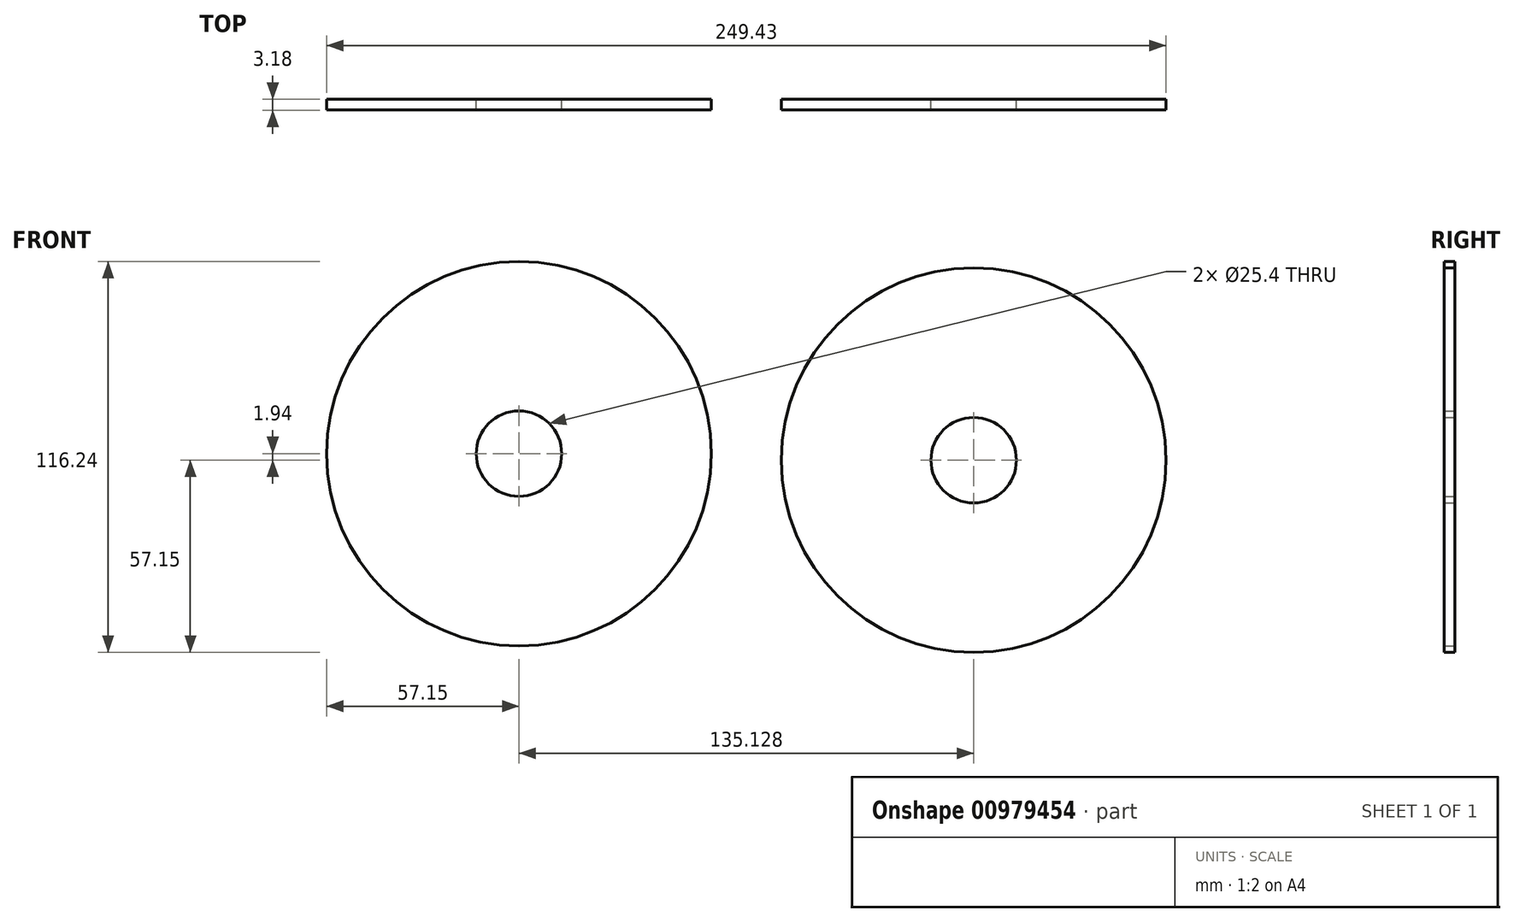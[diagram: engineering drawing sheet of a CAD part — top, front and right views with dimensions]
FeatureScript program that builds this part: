
annotation { "Feature Type Name" : "Feature", "Feature Type Description" : "" }
export const myFeature = defineFeature(function(context is Context, id is Id, definition is map)
    precondition{}
    {
        {
            var Q0;
            Q0=qCreatedBy(makeId("Front.planeOp"),FACE);
            var sketch = newSketch(context, id + "F0", { "sketchPlane" : qUnion([Q0])});
            skCircle(sketch, "E0", {"center": v(0, 0) * mm, "radius": 57.15 * mm});
            skLineSegment(sketch, "E1", {"start": v(-32.13, 47.26) * mm, "end": v(-11.2, 16.47) * mm});
            skLineSegment(sketch, "E2", {"start": v(6.27, 18.9) * mm, "end": v(18, 54.24) * mm});
            skLineSegment(sketch, "E3", {"start": v(18, 54.24) * mm, "end": v(6.27, 18.9) * mm});
            skLineSegment(sketch, "E4", {"start": v(10.46, -16.95) * mm, "end": v(24.43, -51.66) * mm});
            skLineSegment(sketch, "E5", {"start": v(24.43, -51.66) * mm, "end": v(10.46, -16.95) * mm});
            skLineSegment(sketch, "E6", {"start": v(-19.91, 0) * mm, "end": v(-57.15, 0) * mm});
            skLineSegment(sketch, "E7", {"start": v(-57.15, 0) * mm, "end": v(-19.91, 0) * mm});
            skLineSegment(sketch, "E8", {"start": v(19.91, 0) * mm, "end": v(57.15, 0) * mm});
            skLineSegment(sketch, "E9", {"start": v(57.15, 0) * mm, "end": v(19.91, 0) * mm});
            skLineSegment(sketch, "E10", {"start": v(-9.2, -17.66) * mm, "end": v(-27.3, -50.21) * mm});
            skLineSegment(sketch, "E11", {"start": v(-27.3, -50.21) * mm, "end": v(-9.2, -17.66) * mm});
            skCircle(sketch, "E12", {"center": v(135.13, -1.94) * mm, "radius": 57.15 * mm});
            skLineSegment(sketch, "E13", {"start": v(103, 45.32) * mm, "end": v(123.93, 14.53) * mm});
            skLineSegment(sketch, "E14", {"start": v(141.4, 16.96) * mm, "end": v(153.12, 52.3) * mm});
            skLineSegment(sketch, "E15", {"start": v(153.12, 52.3) * mm, "end": v(141.4, 16.96) * mm});
            skLineSegment(sketch, "E16", {"start": v(145.58, -18.89) * mm, "end": v(159.56, -53.6) * mm});
            skLineSegment(sketch, "E17", {"start": v(159.56, -53.6) * mm, "end": v(145.58, -18.89) * mm});
            skLineSegment(sketch, "E18", {"start": v(115.22, -1.94) * mm, "end": v(77.98, -1.94) * mm});
            skLineSegment(sketch, "E19", {"start": v(77.98, -1.94) * mm, "end": v(115.22, -1.94) * mm});
            skLineSegment(sketch, "E20", {"start": v(155.04, -1.94) * mm, "end": v(192.28, -1.94) * mm});
            skLineSegment(sketch, "E21", {"start": v(192.28, -1.94) * mm, "end": v(155.04, -1.94) * mm});
            skLineSegment(sketch, "E22", {"start": v(125.93, -19.6) * mm, "end": v(107.84, -52.15) * mm});
            skLineSegment(sketch, "E23", {"start": v(107.84, -52.15) * mm, "end": v(125.93, -19.6) * mm});
            skCircle(sketch, "E24", {"center": v(0, 0) * mm, "radius": 12.7 * mm});
            skCircle(sketch, "E25", {"center": v(135.13, -1.94) * mm, "radius": 12.7 * mm});
            skSolve(sketch);
        }
        {
            var Q0;
            Q0=makeQuery(id+"F0.imprint","IMPRINT",FACE,{"disambiguationData":[TD([[makeQuery(id+"F0.imprint","IMPRINT",EDGE,{"derivedFrom":sQuery(id+"F0.wireOp",EDGE,"E24")}),-1.0]])]});
            var Q1;
            Q1=makeQuery(id+"F0.imprint","IMPRINT",FACE,{"disambiguationData":[TD([[makeQuery(id+"F0.imprint","IMPRINT",EDGE,{"derivedFrom":sQuery(id+"F0.wireOp",EDGE,"E25")}),-1.0]])]});
            extrude(context, id + "F1", {"entities" : qUnion([Q0, Q1]), "depth" : 3.17 * mm, "offsetDistance" : 25.4 * mm});
        }
    });
